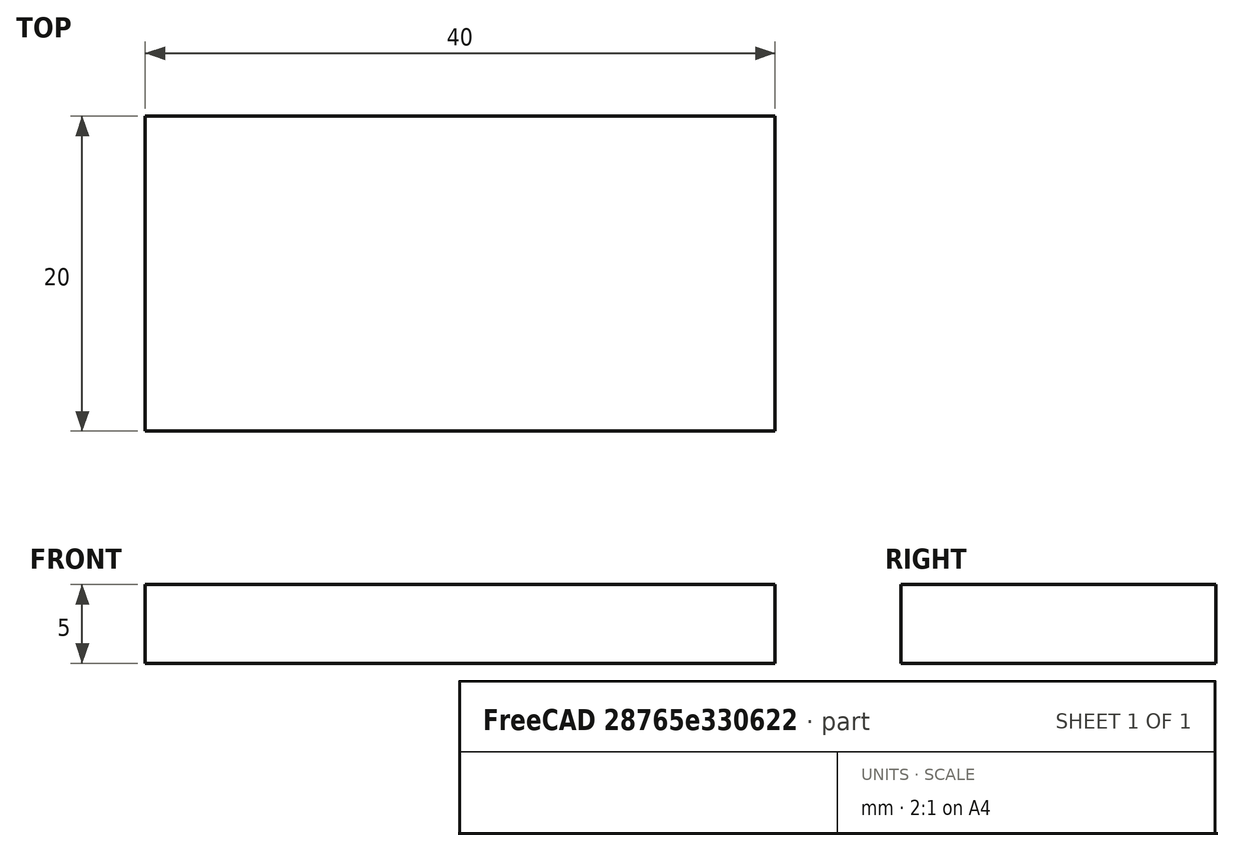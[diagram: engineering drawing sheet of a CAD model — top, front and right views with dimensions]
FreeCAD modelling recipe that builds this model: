
FCSTD DOCUMENT  (FreeCAD 0.20R29410 (Git))
Label: cubo_boceto
License: All rights reserved
LicenseURL: http://en.wikipedia.org/wiki/All_rights_reserved
objects: Sketcher::SketchObject×1, Part::Extrusion×1
note: 2 computed .brp shape members not serialized (recipe doc carries the construction recipe); baked Part::Feature solids carry a one-line shape summary decoded from their .brp

FEATURE [Sketcher::SketchObject] Sketch
  FullyConstrained = true
  sketch-geometry (4):
    g0: LineSegment StartX=-40 StartY=20 StartZ=0 EndX=0 EndY=20 EndZ=0
    g1: LineSegment StartX=0 StartY=20 StartZ=0 EndX=0 EndY=0 EndZ=0
    g2: LineSegment StartX=-40 StartY=20 StartZ=0 EndX=-40 EndY=0 EndZ=0
    g3: LineSegment StartX=-40 StartY=0 StartZ=0 EndX=0 EndY=0 EndZ=0
  constraints (11):
    c: Coincident(g1,g0)
    c: Coincident(g3,g1)
    c: Coincident(g3,g2)
    c: Coincident(g2,g0)
    c: Horizontal(g3)
    c: Vertical(g2)
    c: Horizontal(g0)
    c: Vertical(g1)
    c: DistanceX(g0,g0) = 40  'LX'
    c: DistanceY(g1,g1) = 20  'LY'
    c: Coincident(g1,g-1)
FEATURE [Part::Extrusion] Extrude
  Base = -> Sketch
  Dir = (0,0,1)
  DirMode = 2
  FaceMakerClass = Part::FaceMakerBullseye
  LengthFwd = 5
  LengthRev = 0
  Solid = true
  Symmetric = false
